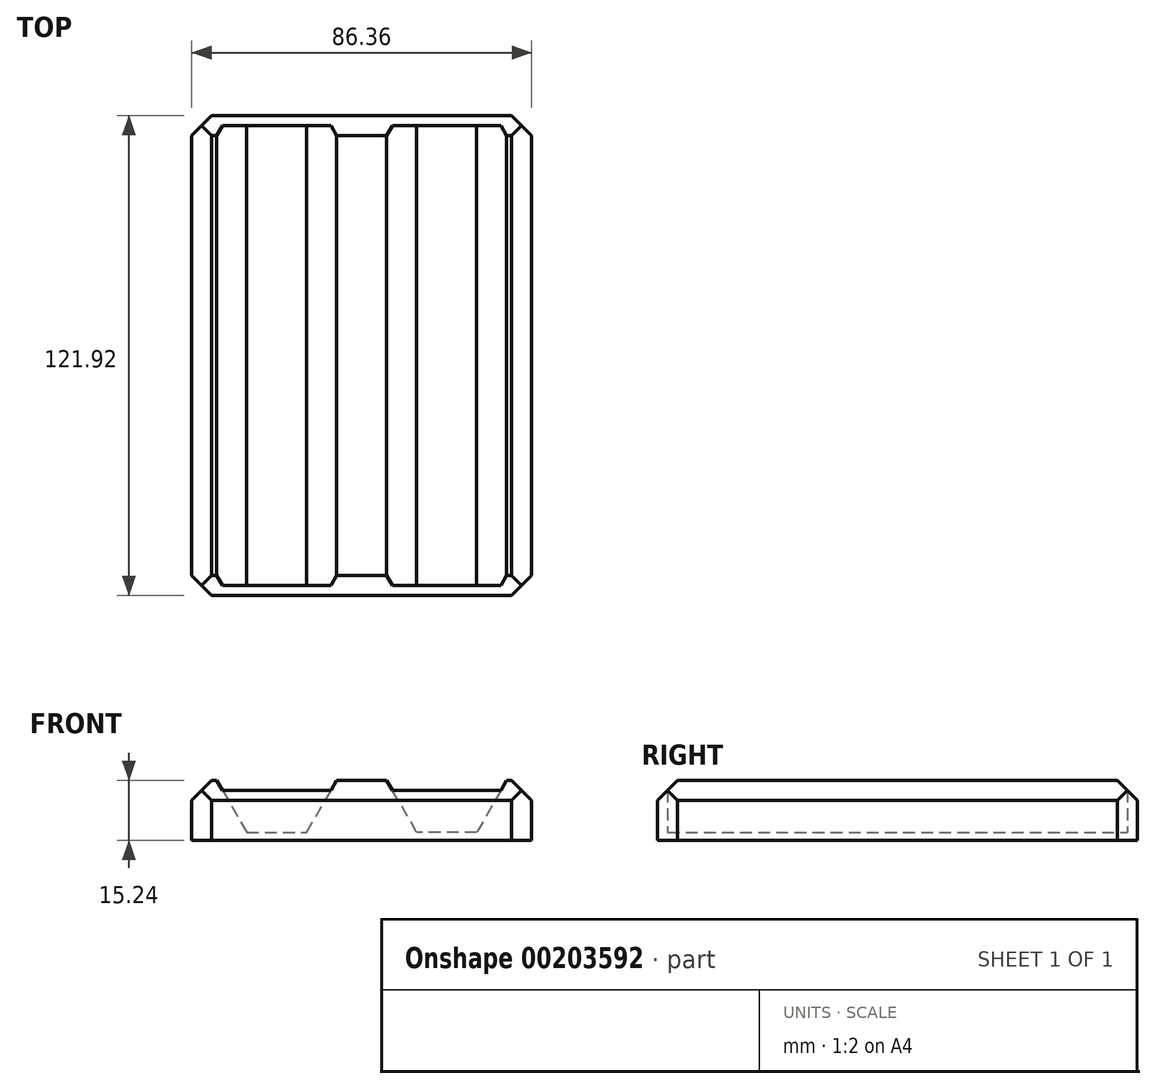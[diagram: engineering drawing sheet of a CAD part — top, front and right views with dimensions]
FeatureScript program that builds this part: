
annotation { "Feature Type Name" : "Feature", "Feature Type Description" : "" }
export const myFeature = defineFeature(function(context is Context, id is Id, definition is map)
    precondition{}
    {
        {
            var Q0;
            Q0=qCreatedBy(makeId("Front.planeOp"),FACE);
            var sketch = newSketch(context, id + "F0", { "sketchPlane" : qUnion([Q0])});
            skLineSegment(sketch, "E0.2", {"start": v(36.83, 0) * mm, "end": v(29.21, -13.2) * mm});
            skLineSegment(sketch, "E0.3", {"start": v(29.21, -13.2) * mm, "end": v(13.97, -13.2) * mm});
            skLineSegment(sketch, "E0.4", {"start": v(13.97, -13.2) * mm, "end": v(6.35, 0) * mm});
            skLineSegment(sketch, "E1", {"start": v(6.35, 0) * mm, "end": v(0, 0) * mm});
            skLineSegment(sketch, "E2", {"start": v(36.83, 0) * mm, "end": v(43.18, 0) * mm});
            skLineSegment(sketch, "E3", {"start": v(43.18, 0) * mm, "end": v(43.18, -15.24) * mm});
            skLineSegment(sketch, "E4", {"start": v(43.18, -15.24) * mm, "end": v(0, -15.24) * mm});
            skLineSegment(sketch, "E5.MirrorCS", {"start": v(-43.18, -15.24) * mm, "end": v(0, -15.24) * mm});
            skLineSegment(sketch, "E6.MirrorCS", {"start": v(-36.83, 0) * mm, "end": v(-43.18, 0) * mm});
            skLineSegment(sketch, "E7.MirrorCS", {"start": v(-6.35, 0) * mm, "end": v(0, 0) * mm});
            skLineSegment(sketch, "E8.MirrorCS", {"start": v(-29.21, -13.2) * mm, "end": v(-13.97, -13.2) * mm});
            skLineSegment(sketch, "E9.MirrorCS", {"start": v(-43.18, 0) * mm, "end": v(-43.18, -15.24) * mm});
            skLineSegment(sketch, "E10.MirrorCS", {"start": v(-36.83, 0) * mm, "end": v(-29.21, -13.2) * mm});
            skLineSegment(sketch, "E11.MirrorCS", {"start": v(-13.97, -13.2) * mm, "end": v(-6.35, 0) * mm});
            skSolve(sketch);
        }
        {
            var Q0;
            Q0=makeQuery(id+"F0.imprint","IMPRINT",FACE,{"disambiguationData":[TD([[makeQuery(id+"F0.imprint","IMPRINT",EDGE,{"derivedFrom":sQuery(id+"F0.wireOp",EDGE,"E0.2")}),1.0]])]});
            extrude(context, id + "F1", {"entities" : qUnion([Q0]), "depth" : 116.84 * mm});
        }
        {
            var Q0;
            Q0=makeQuery(id+"F1.opExtrude","CAP_FACE",FACE,{"disambiguationData":[OSD([sQuery(id+"F0.wireOp",EDGE,"E0.2"),sQuery(id+"F0.wireOp",EDGE,"E0.3"),sQuery(id+"F0.wireOp",EDGE,"E0.4"),sQuery(id+"F0.wireOp",EDGE,"E1"),sQuery(id+"F0.wireOp",EDGE,"E2"),sQuery(id+"F0.wireOp",EDGE,"E3"),sQuery(id+"F0.wireOp",EDGE,"E4"),sQuery(id+"F0.wireOp",EDGE,"E5.MirrorCS"),sQuery(id+"F0.wireOp",EDGE,"E6.MirrorCS"),sQuery(id+"F0.wireOp",EDGE,"E7.MirrorCS"),sQuery(id+"F0.wireOp",EDGE,"E8.MirrorCS"),sQuery(id+"F0.wireOp",EDGE,"E9.MirrorCS"),sQuery(id+"F0.wireOp",EDGE,"E10.MirrorCS"),sQuery(id+"F0.wireOp",EDGE,"E11.MirrorCS")])],"isStart":false});
            var sketch = newSketch(context, id + "F2", { "sketchPlane" : qUnion([Q0])});
            skLineSegment(sketch, "E12.bottom", {"start": v(-43.18, 0) * mm, "end": v(43.18, 0) * mm});
            skLineSegment(sketch, "E12.top", {"start": v(-43.18, -15.24) * mm, "end": v(43.18, -15.24) * mm});
            skLineSegment(sketch, "E12.left", {"start": v(-43.18, 0) * mm, "end": v(-43.18, -15.24) * mm});
            skLineSegment(sketch, "E12.right", {"start": v(43.18, 0) * mm, "end": v(43.18, -15.24) * mm});
            skSolve(sketch);
        }
        {
            var Q0;
            Q0 = qSketchRegion(id + "F2", true);
            extrude(context, id + "F3", {"entities" : qUnion([Q0]), "operationType" : NewBodyOperationType.ADD, "depth" : 2.54 * mm});
        }
        {
            var Q0;
            Q0=makeQuery(id+"F1.opExtrude","CAP_FACE",FACE,{"disambiguationData":[OSD([sQuery(id+"F0.wireOp",EDGE,"E0.2"),sQuery(id+"F0.wireOp",EDGE,"E0.3"),sQuery(id+"F0.wireOp",EDGE,"E0.4"),sQuery(id+"F0.wireOp",EDGE,"E1"),sQuery(id+"F0.wireOp",EDGE,"E2"),sQuery(id+"F0.wireOp",EDGE,"E3"),sQuery(id+"F0.wireOp",EDGE,"E4"),sQuery(id+"F0.wireOp",EDGE,"E5.MirrorCS"),sQuery(id+"F0.wireOp",EDGE,"E6.MirrorCS"),sQuery(id+"F0.wireOp",EDGE,"E7.MirrorCS"),sQuery(id+"F0.wireOp",EDGE,"E8.MirrorCS"),sQuery(id+"F0.wireOp",EDGE,"E9.MirrorCS"),sQuery(id+"F0.wireOp",EDGE,"E10.MirrorCS"),sQuery(id+"F0.wireOp",EDGE,"E11.MirrorCS")])],"isStart":true});
            var sketch = newSketch(context, id + "F4", { "sketchPlane" : qUnion([Q0])});
            skLineSegment(sketch, "E13.bottom", {"start": v(-43.18, 0) * mm, "end": v(43.18, 0) * mm});
            skLineSegment(sketch, "E13.top", {"start": v(-43.18, -15.24) * mm, "end": v(43.18, -15.24) * mm});
            skLineSegment(sketch, "E13.left", {"start": v(-43.18, 0) * mm, "end": v(-43.18, -15.24) * mm});
            skLineSegment(sketch, "E13.right", {"start": v(43.18, 0) * mm, "end": v(43.18, -15.24) * mm});
            skSolve(sketch);
        }
        {
            var Q0;
            Q0 = qSketchRegion(id + "F4", true);
            extrude(context, id + "F5", {"entities" : qUnion([Q0]), "operationType" : NewBodyOperationType.ADD, "depth" : 2.54 * mm});
        }
        {
            var Q0;
            Q0=makeQuery(id+"F5.boolean.opBoolean","MERGE",EDGE,{"derivedFrom":[makeQuery(id+"F3.boolean.opBoolean","MERGE",EDGE,{"derivedFrom":[makeQuery(id+"F1.opExtrude","SWEPT_EDGE",EDGE,{"disambiguationData":[OSD([sQuery(id+"F0.wireOp",EDGE,"E6.MirrorCS"),sQuery(id+"F0.wireOp",EDGE,"E9.MirrorCS")])]}),makeQuery(id+"F3.opExtrude","SWEPT_EDGE",EDGE,{"disambiguationData":[OSD([sQuery(id+"F2.wireOp",EDGE,"E12.bottom"),sQuery(id+"F2.wireOp",EDGE,"E12.left")])]})]}),makeQuery(id+"F5.opExtrude","SWEPT_EDGE",EDGE,{"disambiguationData":[OSD([sQuery(id+"F4.wireOp",EDGE,"E13.bottom"),sQuery(id+"F4.wireOp",EDGE,"E13.right")])]})]});
            var Q1;
            Q1=makeQuery(id+"F3.opExtrude","CAP_EDGE",EDGE,{"disambiguationData":[OSD([sQuery(id+"F2.wireOp",EDGE,"E12.bottom")])],"isStart":false});
            var Q2;
            Q2=makeQuery(id+"F5.boolean.opBoolean","MERGE",EDGE,{"derivedFrom":[makeQuery(id+"F3.boolean.opBoolean","MERGE",EDGE,{"derivedFrom":[makeQuery(id+"F1.opExtrude","SWEPT_EDGE",EDGE,{"disambiguationData":[OSD([sQuery(id+"F0.wireOp",EDGE,"E2"),sQuery(id+"F0.wireOp",EDGE,"E3")])]}),makeQuery(id+"F3.opExtrude","SWEPT_EDGE",EDGE,{"disambiguationData":[OSD([sQuery(id+"F2.wireOp",EDGE,"E12.bottom"),sQuery(id+"F2.wireOp",EDGE,"E12.right")])]})]}),makeQuery(id+"F5.opExtrude","SWEPT_EDGE",EDGE,{"disambiguationData":[OSD([sQuery(id+"F4.wireOp",EDGE,"E13.bottom"),sQuery(id+"F4.wireOp",EDGE,"E13.left")])]})]});
            var Q3;
            Q3=makeQuery(id+"F5.opExtrude","CAP_EDGE",EDGE,{"disambiguationData":[OSD([sQuery(id+"F4.wireOp",EDGE,"E13.bottom")])],"isStart":false});
            chamfer(context, id + "F6", {"entities" : qUnion([Q0, Q1, Q2, Q3]), "width" : 5.08 * mm, "tangentPropagation" : true});
        }
        {
            var Q0;
            Q0=makeQuery(id+"F3.opExtrude","CAP_EDGE",EDGE,{"disambiguationData":[OSD([sQuery(id+"F2.wireOp",EDGE,"E12.left")])],"isStart":false});
            var Q1;
            Q1=makeQuery(id+"F3.opExtrude","CAP_EDGE",EDGE,{"disambiguationData":[OSD([sQuery(id+"F2.wireOp",EDGE,"E12.right")])],"isStart":false});
            var Q2;
            Q2=makeQuery(id+"F5.opExtrude","CAP_EDGE",EDGE,{"disambiguationData":[OSD([sQuery(id+"F4.wireOp",EDGE,"E13.left")])],"isStart":false});
            var Q3;
            Q3=makeQuery(id+"F5.opExtrude","CAP_EDGE",EDGE,{"disambiguationData":[OSD([sQuery(id+"F4.wireOp",EDGE,"E13.right")])],"isStart":false});
            chamfer(context, id + "F7", {"entities" : qUnion([Q0, Q1, Q2, Q3]), "width" : 5.08 * mm, "tangentPropagation" : true});
        }
    });
